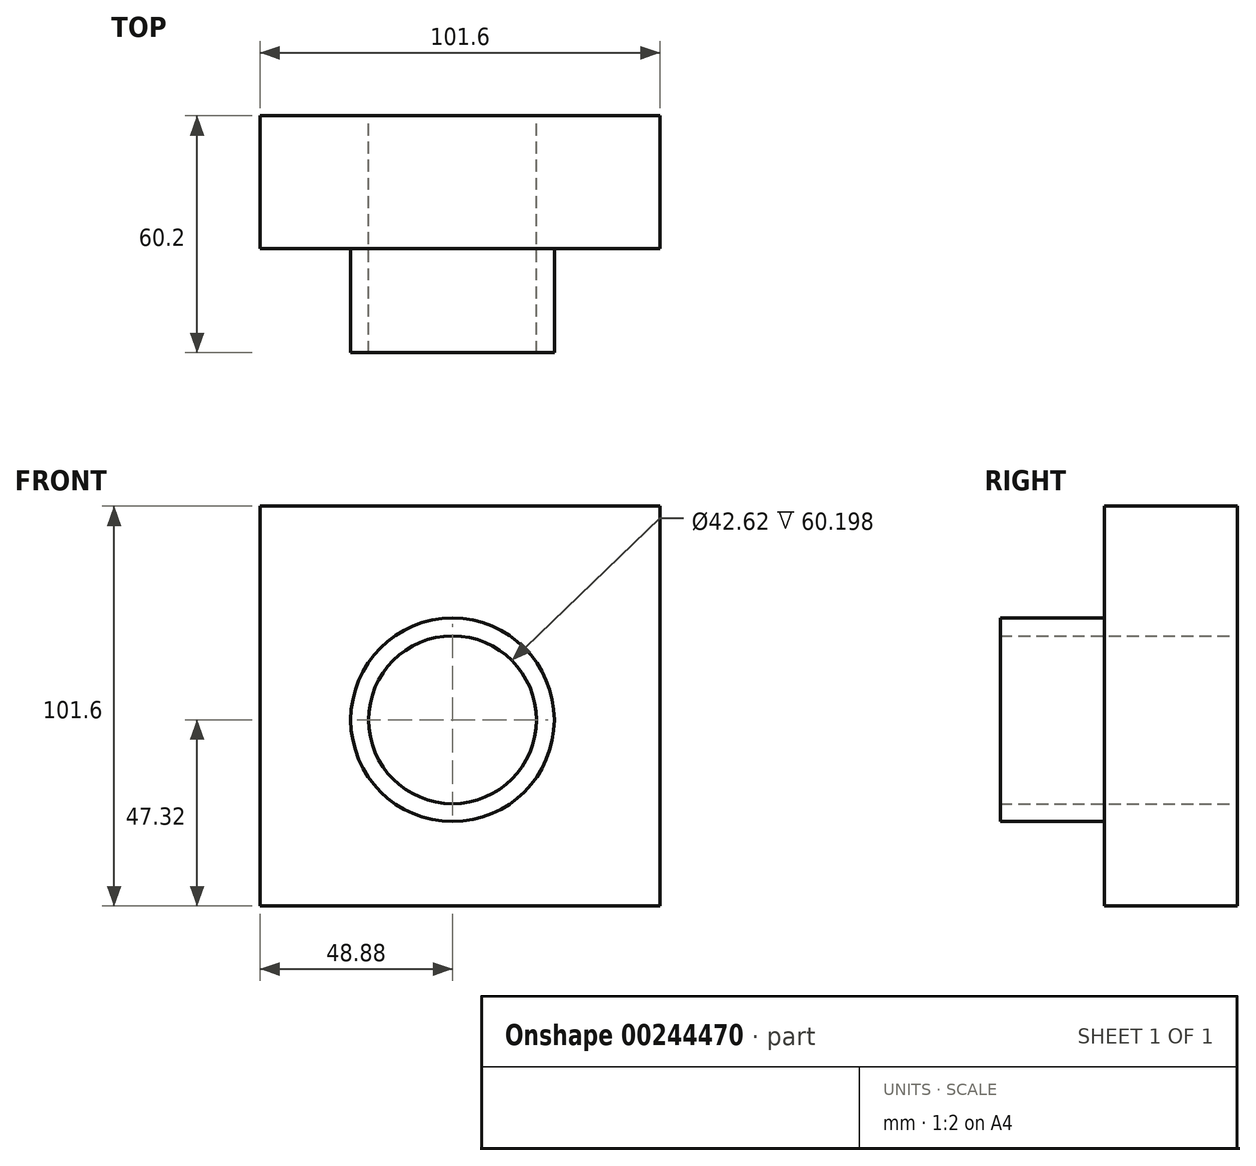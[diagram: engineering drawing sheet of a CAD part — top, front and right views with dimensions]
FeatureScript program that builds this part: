
annotation { "Feature Type Name" : "Feature", "Feature Type Description" : "" }
export const myFeature = defineFeature(function(context is Context, id is Id, definition is map)
    precondition{}
    {
        {
            var Q0;
            Q0=qCreatedBy(makeId("Front.planeOp"),FACE);
            var sketch = newSketch(context, id + "F0", { "sketchPlane" : qUnion([Q0])});
            skLineSegment(sketch, "E0.bottom", {"start": v(-48.88, 54.28) * mm, "end": v(52.72, 54.28) * mm});
            skLineSegment(sketch, "E0.top", {"start": v(-48.88, -47.32) * mm, "end": v(52.72, -47.32) * mm});
            skLineSegment(sketch, "E0.left", {"start": v(-48.88, 54.28) * mm, "end": v(-48.88, -47.32) * mm});
            skLineSegment(sketch, "E0.right", {"start": v(52.72, 54.28) * mm, "end": v(52.72, -47.32) * mm});
            skCircle(sketch, "E1", {"center": v(0, 0) * mm, "radius": 21.31 * mm});
            skCircle(sketch, "E2", {"center": v(0, 0) * mm, "radius": 25.85 * mm});
            skSolve(sketch);
        }
        {
            var Q0;
            Q0 = qSketchRegion(id + "F0", true);
            extrude(context, id + "F1", {"entities" : qUnion([Q0]), "depth" : 25.4 * mm});
        }
        {
            var Q0;
            Q0=makeQuery(id+"F0.imprint","IMPRINT",FACE,{"disambiguationData":[TD([[makeQuery(id+"F0.imprint","IMPRINT",EDGE,{"derivedFrom":sQuery(id+"F0.wireOp",EDGE,"E1")}),-1.0]])]});
            extrude(context, id + "F2", {"entities" : qUnion([Q0]), "operationType" : NewBodyOperationType.ADD, "depth" : 60.2 * mm});
        }
        {
            var Q0;
            Q0=makeQuery(id+"F1.opExtrude","CAP_FACE",FACE,{"disambiguationData":[OSD([sQuery(id+"F0.wireOp",EDGE,"E0.bottom"),sQuery(id+"F0.wireOp",EDGE,"E0.top"),sQuery(id+"F0.wireOp",EDGE,"E0.left"),sQuery(id+"F0.wireOp",EDGE,"E0.right"),sQuery(id+"F0.wireOp",EDGE,"E2")])],"isStart":false});
            extrude(context, id + "F3", {"entities" : qUnion([Q0]), "operationType" : NewBodyOperationType.ADD, "depth" : 8.38 * mm});
        }
    });
